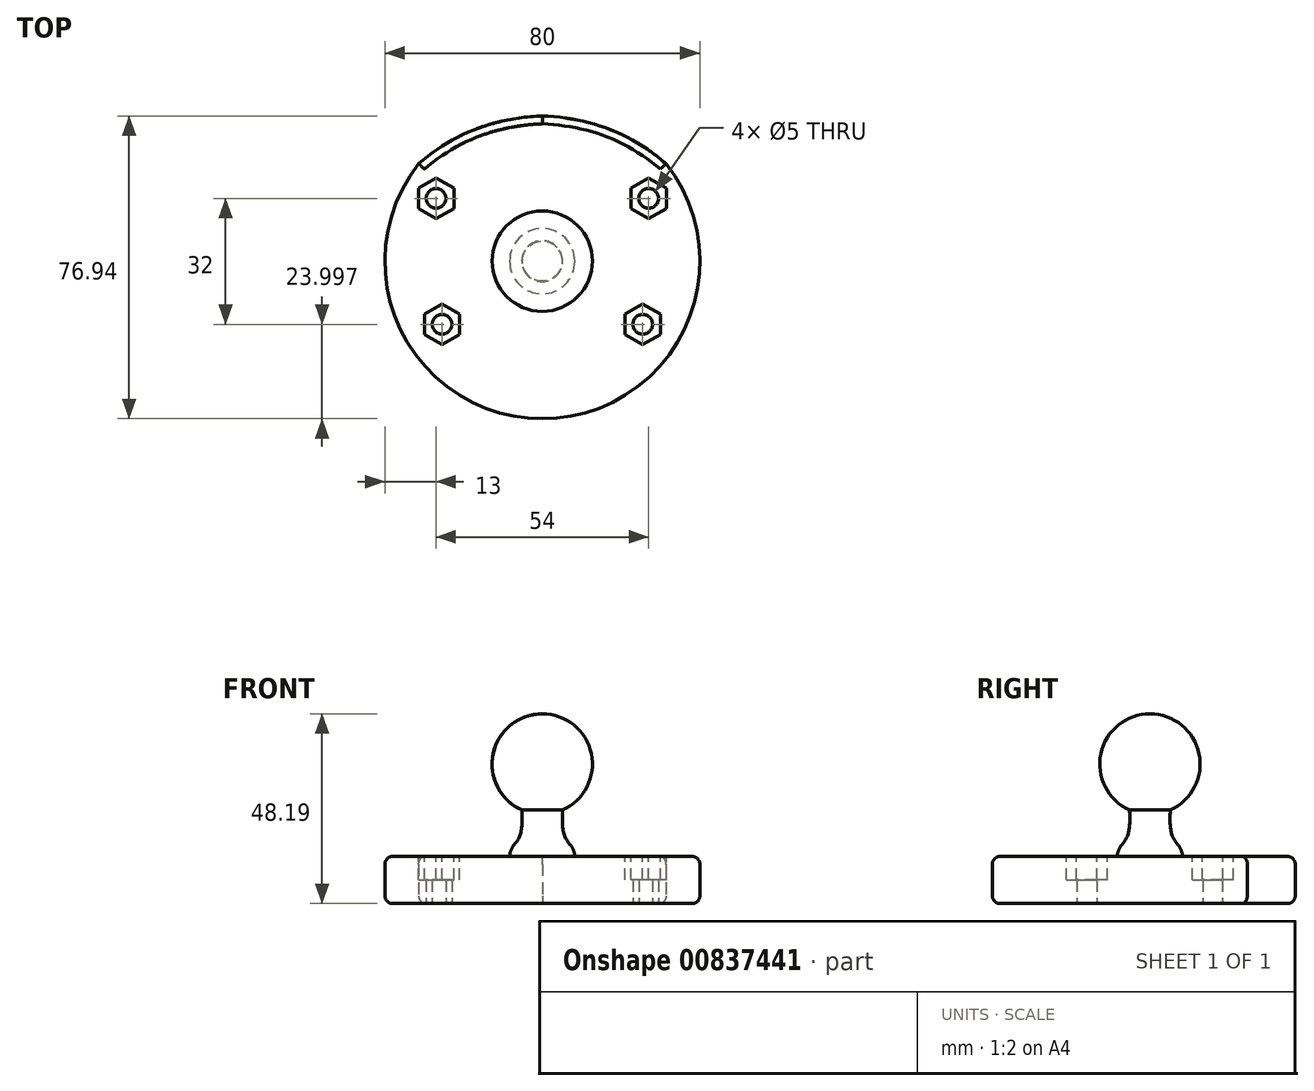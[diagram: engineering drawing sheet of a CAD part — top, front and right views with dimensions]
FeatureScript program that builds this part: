
annotation { "Feature Type Name" : "Feature", "Feature Type Description" : "" }
export const myFeature = defineFeature(function(context is Context, id is Id, definition is map)
    precondition{}
    {
        {
            var Q0;
            Q0=qCreatedBy(makeId("Top.planeOp"),FACE);
            var sketch = newSketch(context, id + "F0", { "sketchPlane" : qUnion([Q0])});
            skPoint(sketch, "E0.middle", {"position": v(0.04, -0.03) * mm});
            skPoint(sketch, "E1.start.orphan", {"position": v(0.04, -40.03) * mm});
            skPoint(sketch, "E2.visualSharp", {"position": v(34.29, 20.63) * mm});
            skPoint(sketch, "E3.visualSharp", {"position": v(-34.53, 20.09) * mm});
            skPoint(sketch, "E4.start.orphan", {"position": v(27.04, -16.03) * mm});
            skPoint(sketch, "E5.start.orphan", {"position": v(-26.96, -16.03) * mm});
            skCircle(sketch, "E6", {"center": v(25.54, -16.03) * mm, "radius": 2.5 * mm});
            skCircle(sketch, "E7", {"center": v(-25.46, -16.03) * mm, "radius": 2.5 * mm});
            skPoint(sketch, "E8.center.orphan", {"position": v(27.04, 15.97) * mm});
            skCircle(sketch, "E9", {"center": v(27.04, 15.97) * mm, "radius": 2.5 * mm});
            skCircle(sketch, "E10", {"center": v(-26.96, 15.97) * mm, "radius": 2.5 * mm});
            skArc(sketch, "E11", {"start": v(-34.53, 20.09) * mm, "mid": v(0.36, -40.03) * mm, "end": v(34.29, 20.63) * mm});
            skPoint(sketch, "E12.endSnap0", {"position": v(0.04, 24.74) * mm});
            skPoint(sketch, "E13.orphan", {"position": v(0.04, 39.97) * mm});
            skPoint(sketch, "E14.visualSharp", {"position": v(31.44, 24.74) * mm});
            skPoint(sketch, "E15.visualSharp", {"position": v(-31.37, 24.74) * mm});
            skLineSegment(sketch, "E16", {"start": v(0.04, -0.03) * mm, "end": v(0.04, 39.97) * mm});
            skArc(sketch, "E17", {"start": v(-31.37, 24.74) * mm, "mid": v(0.04, -40.03) * mm, "end": v(31.44, 24.74) * mm});
            skFitSpline(sketch, "E18", {"points": [v(-31.37, 24.74) * mm, v(0.04, 36.91) * mm, v(31.44, 24.74) * mm], "startDerivative": vector(50.74, 44.21) * mm, "endDerivative": vector(11.96, -59.12) * mm});
            skFitSpline(sketch, "E19.MirrorCS", {"points": [v(31.44, 24.74) * mm, v(0.04, 36.91) * mm, v(-31.37, 24.74) * mm], "startDerivative": vector(-50.74, 44.21) * mm, "endDerivative": vector(-11.96, -59.12) * mm});
            skSolve(sketch);
        }
        {
            var Q0;
            Q0=makeQuery(id+"F0.imprint","IMPRINT",FACE,{"disambiguationData":[TD([[makeQuery(id+"F0.imprint","IMPRINT",EDGE,{"derivedFrom":sQuery(id+"F0.wireOp",EDGE,"E6")}),-1.0]])]});
            extrude(context, id + "F1", {"entities" : qUnion([Q0]), "depth" : 12 * mm, "offsetDistance" : 25 * mm});
        }
        {
            var Q0;
            Q0=qCreatedBy(makeId("Front.planeOp"),FACE);
            var sketch = newSketch(context, id + "F2", { "sketchPlane" : qUnion([Q0])});
            skLineSegment(sketch, "E20", {"start": v(0, 0) * mm, "end": v(0, 101.07) * mm});
            skSolve(sketch);
        }
        {
            var Q0;
            Q0=makeQuery(id+"F1.opExtrude","CAP_FACE",FACE,{"disambiguationData":[OSD([sQuery(id+"F0.wireOp",EDGE,"E6"),sQuery(id+"F0.wireOp",EDGE,"E7"),sQuery(id+"F0.wireOp",EDGE,"E9"),sQuery(id+"F0.wireOp",EDGE,"E10"),sQuery(id+"F0.wireOp",EDGE,"E17"),sQuery(id+"F0.wireOp",EDGE,"E18"),sQuery(id+"F0.wireOp",EDGE,"E19.MirrorCS")])],"isStart":false});
            var sketch = newSketch(context, id + "F3", { "sketchPlane" : qUnion([Q0])});
            skCircle(sketch, "E21.cCircle", {"center": v(-26.96, 15.97) * mm, "radius": 4.5 * mm, "construction": true});
            skLineSegment(sketch, "E21.0", {"start": v(-22.46, 18.56) * mm, "end": v(-22.46, 13.37) * mm});
            skLineSegment(sketch, "E21.1", {"start": v(-22.46, 13.37) * mm, "end": v(-26.96, 10.77) * mm});
            skLineSegment(sketch, "E21.2", {"start": v(-26.96, 10.77) * mm, "end": v(-31.46, 13.37) * mm});
            skLineSegment(sketch, "E21.3", {"start": v(-31.46, 13.37) * mm, "end": v(-31.46, 18.56) * mm});
            skLineSegment(sketch, "E21.4", {"start": v(-31.46, 18.56) * mm, "end": v(-26.96, 21.16) * mm});
            skLineSegment(sketch, "E21.5", {"start": v(-26.96, 21.16) * mm, "end": v(-22.46, 18.56) * mm});
            skPoint(sketch, "E21.0.midPoint", {"position": v(-22.46, 15.97) * mm});
            skCircle(sketch, "E22.cCircle", {"center": v(27.04, 15.97) * mm, "radius": 4.5 * mm, "construction": true});
            skLineSegment(sketch, "E22.0", {"start": v(22.54, 13.37) * mm, "end": v(22.54, 18.56) * mm});
            skLineSegment(sketch, "E22.1", {"start": v(22.54, 18.56) * mm, "end": v(27.04, 21.16) * mm});
            skLineSegment(sketch, "E22.2", {"start": v(27.04, 21.16) * mm, "end": v(31.54, 18.56) * mm});
            skLineSegment(sketch, "E22.3", {"start": v(31.54, 18.56) * mm, "end": v(31.54, 13.37) * mm});
            skLineSegment(sketch, "E22.4", {"start": v(31.54, 13.37) * mm, "end": v(27.04, 10.77) * mm});
            skLineSegment(sketch, "E22.5", {"start": v(27.04, 10.77) * mm, "end": v(22.54, 13.37) * mm});
            skPoint(sketch, "E22.0.midPoint", {"position": v(22.54, 15.97) * mm});
            skCircle(sketch, "E23.cCircle", {"center": v(25.54, -16.03) * mm, "radius": 4.5 * mm, "construction": true});
            skLineSegment(sketch, "E23.0", {"start": v(21.04, -18.63) * mm, "end": v(21.04, -13.44) * mm});
            skLineSegment(sketch, "E23.1", {"start": v(21.04, -13.44) * mm, "end": v(25.54, -10.84) * mm});
            skLineSegment(sketch, "E23.2", {"start": v(25.54, -10.84) * mm, "end": v(30.04, -13.44) * mm});
            skLineSegment(sketch, "E23.3", {"start": v(30.04, -13.44) * mm, "end": v(30.04, -18.63) * mm});
            skLineSegment(sketch, "E23.4", {"start": v(30.04, -18.63) * mm, "end": v(25.54, -21.23) * mm});
            skLineSegment(sketch, "E23.5", {"start": v(25.54, -21.23) * mm, "end": v(21.04, -18.63) * mm});
            skPoint(sketch, "E23.0.midPoint", {"position": v(21.04, -16.03) * mm});
            skCircle(sketch, "E24.cCircle", {"center": v(-25.46, -16.03) * mm, "radius": 4.5 * mm, "construction": true});
            skLineSegment(sketch, "E24.0", {"start": v(-20.96, -13.44) * mm, "end": v(-20.96, -18.63) * mm});
            skLineSegment(sketch, "E24.1", {"start": v(-20.96, -18.63) * mm, "end": v(-25.46, -21.23) * mm});
            skLineSegment(sketch, "E24.2", {"start": v(-25.46, -21.23) * mm, "end": v(-29.96, -18.63) * mm});
            skLineSegment(sketch, "E24.3", {"start": v(-29.96, -18.63) * mm, "end": v(-29.96, -13.44) * mm});
            skLineSegment(sketch, "E24.4", {"start": v(-29.96, -13.44) * mm, "end": v(-25.46, -10.84) * mm});
            skLineSegment(sketch, "E24.5", {"start": v(-25.46, -10.84) * mm, "end": v(-20.96, -13.44) * mm});
            skPoint(sketch, "E24.0.midPoint", {"position": v(-20.96, -16.03) * mm});
            skSolve(sketch);
        }
        {
            var Q0;
            Q0=makeQuery(id+"F3.imprint","IMPRINT",FACE,{"disambiguationData":[TD([[makeQuery(id+"F3.imprint","IMPRINT",EDGE,{"derivedFrom":sQuery(id+"F3.wireOp",EDGE,"E21.0")}),-1.0]])]});
            var Q1;
            Q1=makeQuery(id+"F3.imprint","IMPRINT",FACE,{"disambiguationData":[TD([[makeQuery(id+"F3.imprint","IMPRINT",EDGE,{"derivedFrom":sQuery(id+"F3.wireOp",EDGE,"E22.0")}),-1.0]])]});
            var Q2;
            Q2=makeQuery(id+"F3.imprint","IMPRINT",FACE,{"disambiguationData":[TD([[makeQuery(id+"F3.imprint","IMPRINT",EDGE,{"derivedFrom":sQuery(id+"F3.wireOp",EDGE,"E23.0")}),-1.0]])]});
            var Q3;
            Q3=makeQuery(id+"F3.imprint","IMPRINT",FACE,{"disambiguationData":[TD([[makeQuery(id+"F3.imprint","IMPRINT",EDGE,{"derivedFrom":sQuery(id+"F3.wireOp",EDGE,"E24.0")}),-1.0]])]});
            extrude(context, id + "F4", {"entities" : qUnion([Q0, Q1, Q2, Q3]), "operationType" : NewBodyOperationType.REMOVE, "oppositeDirection" : true, "depth" : 6 * mm, "offsetDistance" : 25 * mm});
        }
        {
            var Q0;
            Q0=qCreatedBy(makeId("Front.planeOp"),FACE);
            var sketch = newSketch(context, id + "F5", { "sketchPlane" : qUnion([Q0])});
            skLineSegment(sketch, "E25", {"start": v(0, 0.9) * mm, "end": v(0, 52.27) * mm});
            skLineSegment(sketch, "E26", {"start": v(0, 11.9) * mm, "end": v(-8.28, 11.9) * mm});
            skLineSegment(sketch, "E27", {"start": v(-8.28, 11.9) * mm, "end": v(-8.28, 13.69) * mm});
            skArc(sketch, "E28", {"start": v(-6.02, 46.68) * mm, "mid": v(-12.74, 34.97) * mm, "end": v(-5.18, 23.79) * mm});
            skFitSpline(sketch, "E29", {"points": [v(-8.28, 13.69) * mm, v(-5.65, 17.32) * mm, v(-5.18, 23.79) * mm], "startDerivative": vector(6.91, 7.13) * mm, "endDerivative": vector(-0.46, 12.91) * mm});
            skPoint(sketch, "E30.orphan", {"position": v(0, 48.2) * mm});
            skArc(sketch, "E31", {"start": v(0, 48.2) * mm, "mid": v(-12.47, 38.09) * mm, "end": v(-5.18, 23.79) * mm});
            skPoint(sketch, "E32.end.orphan", {"position": v(0, 46.68) * mm});
            skSolve(sketch);
        }
        {
            var Q0;
            {var subQ1=sQuery(id+"F5.wireOp",EDGE,"E26");Q0=makeQuery(id+"F5.imprint","IMPRINT",FACE,{"disambiguationData":[TD([[makeQuery(id+"F5.imprint","IMPRINT",EDGE,{"derivedFrom":subQ1}),-1.0]])]});}
            var Q1;
            Q1=sQuery(id+"F2.wireOp",EDGE,"E20");
            revolve(context, id + "F6", {"operationType" : NewBodyOperationType.ADD, "surfaceOperationType" : NewSurfaceOperationType.NEW, "entities" : qUnion([Q0]), "axis" : qUnion([Q1]), "revolveType" : RevolveType.FULL});
        }
        {
            var Q0;
            Q0=makeQuery(id+"F6.opRevolve","SWEPT_EDGE",EDGE,{"disambiguationData":[OSD([sQuery(id+"F5.wireOp",EDGE,"E27"),sQuery(id+"F5.wireOp",EDGE,"E29")])]});
            fillet(context, id + "F7", {"entities" : qUnion([Q0]), "radius" : 5 * mm, "tangentPropagation" : true, "allowEdgeOverflow" : false});
        }
        {
            var Q0;
            Q0=makeQuery(id+"F1.opExtrude","CAP_EDGE",EDGE,{"disambiguationData":[OSD([sQuery(id+"F0.wireOp",EDGE,"E17")])],"isStart":false});
            var Q1;
            Q1=makeQuery(id+"F1.opExtrude","CAP_EDGE",EDGE,{"disambiguationData":[OSD([sQuery(id+"F0.wireOp",EDGE,"E17")])],"isStart":true});
            var Q2;
            Q2=makeQuery(id+"F1.opExtrude","CAP_EDGE",EDGE,{"disambiguationData":[OSD([sQuery(id+"F0.wireOp",EDGE,"E19.MirrorCS")])],"isStart":false});
            var Q3;
            Q3=makeQuery(id+"F1.opExtrude","CAP_EDGE",EDGE,{"disambiguationData":[OSD([sQuery(id+"F0.wireOp",EDGE,"E18")])],"isStart":false});
            var Q4;
            Q4=makeQuery(id+"F1.opExtrude","CAP_EDGE",EDGE,{"disambiguationData":[OSD([sQuery(id+"F0.wireOp",EDGE,"E18")])],"isStart":true});
            var Q5;
            Q5=makeQuery(id+"F1.opExtrude","CAP_EDGE",EDGE,{"disambiguationData":[OSD([sQuery(id+"F0.wireOp",EDGE,"E19.MirrorCS")])],"isStart":true});
            fillet(context, id + "F8", {"entities" : qUnion([Q0, Q1, Q2, Q3, Q4, Q5]), "radius" : 2 * mm, "tangentPropagation" : true, "allowEdgeOverflow" : false});
        }
    });
